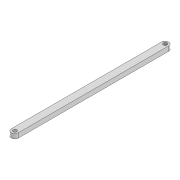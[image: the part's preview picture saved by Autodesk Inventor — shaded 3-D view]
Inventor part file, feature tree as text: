
AUTODESK INVENTOR PART (.ipt)
format: ipt  version: 2022 (Build 260153000, 153)  size: 86,528 bytes
history: native  units: mm
features: extrude x1, sketch x1
ambient origin geometry x8: Origin, YZ Plane, XZ Plane, XY Plane, X Axis, Y Axis, Z Axis, Center Point
bodies: Solid1 (feature_tree)
feature tree (2):
  extrude  "Extrusion1"  Depth=4.0mm
  sketch  "Sketch1"  dims[d0=3.2mm d1=3.2mm d2=6.0mm d3=128.994mm d6=4.0mm d7=0.0mm]
